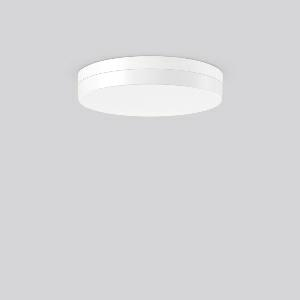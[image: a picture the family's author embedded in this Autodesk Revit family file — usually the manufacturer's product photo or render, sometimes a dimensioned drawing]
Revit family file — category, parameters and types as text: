
# Revit family: flat_slim_round_312675_002_19_1c71
name_source: partatom
category: Lighting Fixtures
units: mm (PartAtom-declared; Revit-internal decimal feet)

## family parameters
Cut with Voids When Loaded = No
Host = Face
Light Source = No
Part Type = Normal
Room Calculation Point = No
Round Connector Dimension = Use Diameter
Shared = No

## types (1)
- MultiLumen 1 830 (1 x LED Modul 830, 2450 lm, 3000)
    Apparent Load = 25 VA
    CIE Flux Codes = 40 70 90 84 100
    Color Rendering = 80
    Color Temperature = 3000
    Default Elevation = 1800 mm
    Height = 75 mm
    Lamp = 1 x LED Modul 830
    Lamp Light Flux = 2450 lm
    Lamp count = 1
    Length = 400 mm
    Lifetime = 50000 h
    Luminous efficacy = 98 lm/W
    Manufacturer = RZB
    ModVariant = No
    Model = 312675.002.19
    Mounting Place = Ceiling
    Mounting Type = Surface mounted
    Number of Poles = 1
    OnlyDefault = Yes
    Power Factor = 1
    Product Name = FLAT SLIM round
    Product group = Surface mounted ceiling and wall luminaires
    ProductGroupID = 305
    Protection Class = Protection class I
    Protection Degree = Degree of protection
    RLX_Detail_Level = 1
    RLX_Emergency_Light_Flux = 0 lm
    RLX_Emergency_Type = 0
    RLX_Emergency_Type_DB = No
    RlxData = <blob elided: 20481 chars, md5=4727b1b1>
    Socket = socket
    Standby Power = 0 W
    System Light Flux = 2450 lm
    System Power = 25 W
    Type Comments = MultiLumen 1 830
    Type Image = 312631.002.jpg
    URL = http://relux.com
    VarID = multilumen_1_830
    Voltage = 0 V
    Weight = 0.00 kg
    Width = 0 mm  [stored 0 ft]

note: [stored X ft] marks values corroborated as IEEE doubles in the binary element streams (Revit-internal decimal feet)

## geometry (parser evidence)
native form markers: Blend x4, Sweep x14
no freeform markers — native parametric forms only
